# Revit family: Poppel - Bracket f wall Post
name_source: partatom
category: Furniture
units: mm (PartAtom-declared; Revit-internal decimal feet)

## family parameters
Always vertical = Yes
Cut with Voids When Loaded = No
OmniClass Number = 23.21.23.13.15
Room Calculation Point = No
Shared = No
Work Plane-Based = No

## types (3) — shared parameters
BIMobject category = Litter Bins
Body material_90 = Steel, Paint Finish, Red
Construction material = Hags - Steel - Galvanized
Edition number = 1
IFC Classification = Furniture
Manufacturer = Hags
Manufacturer name = HAGS
OmniClass Code = 23-21 23 13 15
OmniClass Description = Residential Litter Bins
Product Guid = 90e49432-c870-4a59-897e-b15016e8f9bd
Product SKU = Popel_Detached
Product data url = https://bimobject.com
Product url = https://hags.se
QR code = https://www.hags.com
URL = https://www.hags.com
Uniclass 1.4 Code = L8211
Uniclass 1.4 Description = Furniture
zero-valued in all types: Default Elevation

## per-type parameters (varying)
| type | Body material | Model | Product name |
| 8000125 / Red | Steel, Paint Finish, Red | 8000125 | Poppel Red Bracket f wall Post |
| 8000126 / Green | Steel, Paint Finish, Green | 8000126 | Poppel Green Bracket f wall Post |
| 8000127 / Black | Steel, Paint Finish, Red | 8000127 | Poppel Black Bracket f wall Post |

## geometry (parser evidence)
native form markers: Sweep x2
no freeform markers — native parametric forms only
